# Revit family: LEGRAND_PRISES_NON_VERROUILLEES_ENCASTREES_IP66_400_SYMBOLE
name_source: partatom
category: Annotations génériques
revit_build: Autodesk Revit 2018 (Build: 20170223_1515(x64)
units: mm (PartAtom-declared; Revit-internal decimal feet)

## family parameters
Conserve la lisibilité du texte = Non
Partagée = Non
Rotation avec le composant = Non

## types (9) — shared parameters
2P+T = Non
Prises verrouillées = Non
diamètre symbole = 10 mm  [stored 0.0328084 ft]
rayon pole = 1 mm  [stored 0.00328084 ft]
rayon symbole = 5 mm  [stored 0.0164042 ft]
rayon verrouillage = 0.8 mm  [stored 0.00262467 ft]

## per-type parameters (varying)
| type | 3P+T | 3P+T+N |
| Symbole réf.051131 | Non | Oui |
| Symbole réf.051130 | Oui | Non |
| Symbole réf.051150 | Oui | Non |
| Symbole réf.053050 | Oui | Non |
| Symbole réf.059427 | Oui | Non |
| Symbole réf.059512 | Oui | Non |
| Symbole réf.051151 | Non | Oui |
| Symbole réf.053051 | Non | Oui |
| Symbole réf.059513 | Non | Oui |

note: [stored X ft] marks values corroborated as IEEE doubles in the binary element streams (Revit-internal decimal feet)
